# Revit family: Bath-Island-Caroma Luna 1525
name_source: partatom
category: Plumbing Fixtures
revit_build: Autodesk Revit 2014 (Build: 20140709_2115(x64)
units: mm (PartAtom-declared; Revit-internal decimal feet)

## types (1)
- Standard
    Assembly Code = D2010510
    CW Connection = No
    Capacity_ANZRS = 210.0 L
    Cost = 0 $
    Default Elevation = 0 mm  [stored 0 ft]
    Description = Caroma Luna 1525 Island Bath
    HW Connection = No
    Height_ANZRS = 435 mm  [stored 1.42717 ft]
    Keynote = BT
    Length_ANZRS = 1525 mm  [stored 5.00328 ft]
    Manufacturer = GWA Bathrooms & Kitchens
    Material_ANZRS = Porcelain-White-Caroma
    Model = LN5ISW
    ModifiedIssue_ANZRS = 20170210 $
    PlumbingMaterial_ANZRS = PVC-White-Caroma
    URL = https://specify.caroma.com.au
    Vent Connection = No
    WFU = 2
    Waste = Metal-Brass-Chrome
    Waste Connection = Yes
    Width_ANZRS = 735 mm

note: [stored X ft] marks values corroborated as IEEE doubles in the binary element streams (Revit-internal decimal feet)

## geometry (parser evidence)
native form markers: Blend x9, Sweep x1
no freeform markers — native parametric forms only
